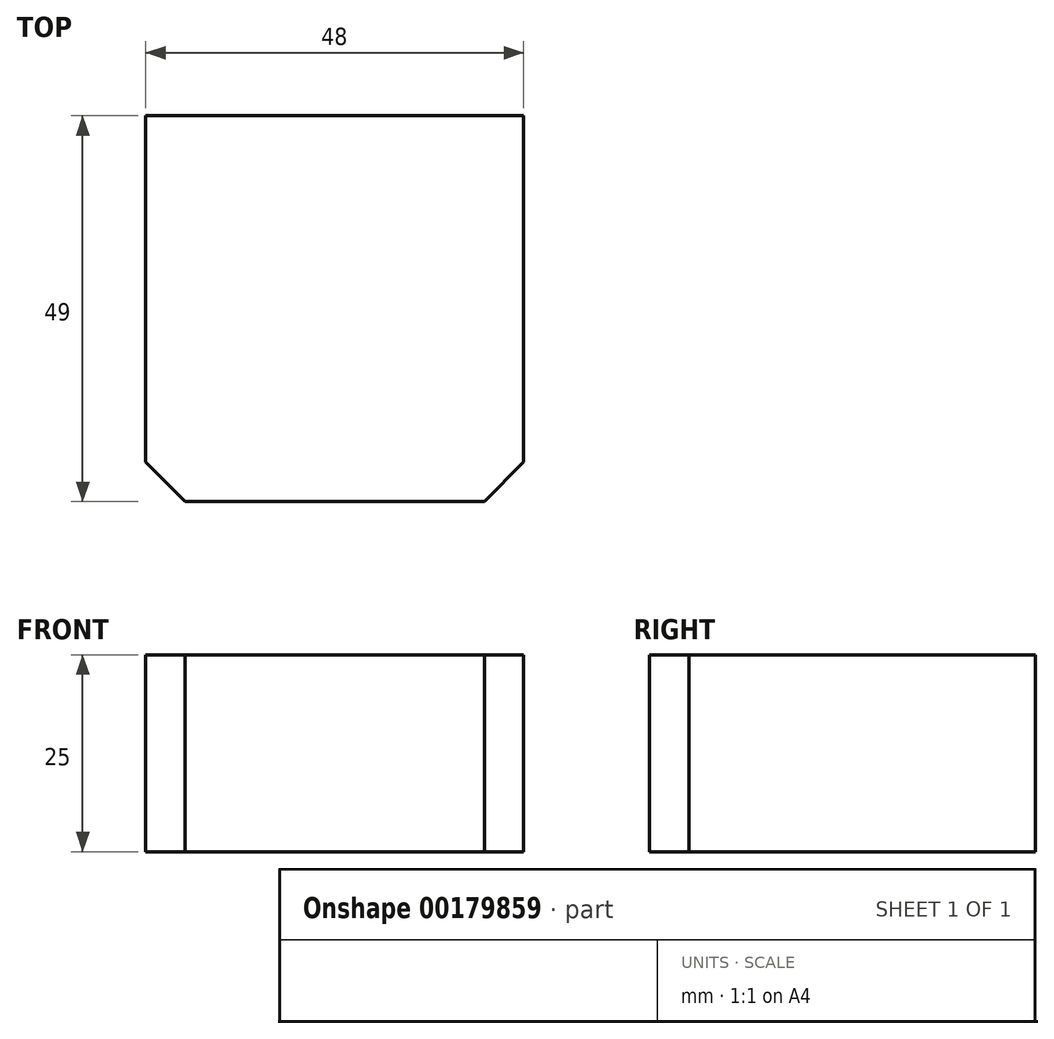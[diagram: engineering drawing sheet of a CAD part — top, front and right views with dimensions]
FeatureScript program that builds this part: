
annotation { "Feature Type Name" : "Feature", "Feature Type Description" : "" }
export const myFeature = defineFeature(function(context is Context, id is Id, definition is map)
    precondition{}
    {
        {
            var Q0;
            Q0=qCreatedBy(makeId("Top.planeOp"),FACE);
            var sketch = newSketch(context, id + "F0", { "sketchPlane" : qUnion([Q0])});
            skLineSegment(sketch, "E0.bottom", {"start": v(-33.14, 31.48) * mm, "end": v(14.86, 31.48) * mm});
            skLineSegment(sketch, "E0.top", {"start": v(-33.14, -17.52) * mm, "end": v(14.86, -17.52) * mm});
            skLineSegment(sketch, "E0.left", {"start": v(-33.14, 31.48) * mm, "end": v(-33.14, -17.52) * mm});
            skLineSegment(sketch, "E0.right", {"start": v(14.86, 31.48) * mm, "end": v(14.86, -17.52) * mm});
            skSolve(sketch);
        }
        {
            var Q0;
            Q0=makeQuery(id+"F0.imprint","IMPRINT",FACE,{"disambiguationData":[TD([[makeQuery(id+"F0.imprint","IMPRINT",EDGE,{"derivedFrom":sQuery(id+"F0.wireOp",EDGE,"E0.bottom")}),-1.0]])]});
            extrude(context, id + "F1", {"entities" : qUnion([Q0]), "depth" : 25 * mm});
        }
        {
            var Q0;
            Q0=makeQuery(id+"F1.opExtrude","SWEPT_EDGE",EDGE,{"disambiguationData":[OSD([sQuery(id+"F0.wireOp",EDGE,"E0.top"),sQuery(id+"F0.wireOp",EDGE,"E0.left")])]});
            var Q1;
            Q1=makeQuery(id+"F1.opExtrude","SWEPT_EDGE",EDGE,{"disambiguationData":[OSD([sQuery(id+"F0.wireOp",EDGE,"E0.top"),sQuery(id+"F0.wireOp",EDGE,"E0.right")])]});
            chamfer(context, id + "F2", {"entities" : qUnion([Q0, Q1]), "width" : 5 * mm, "tangentPropagation" : true});
        }
    });
